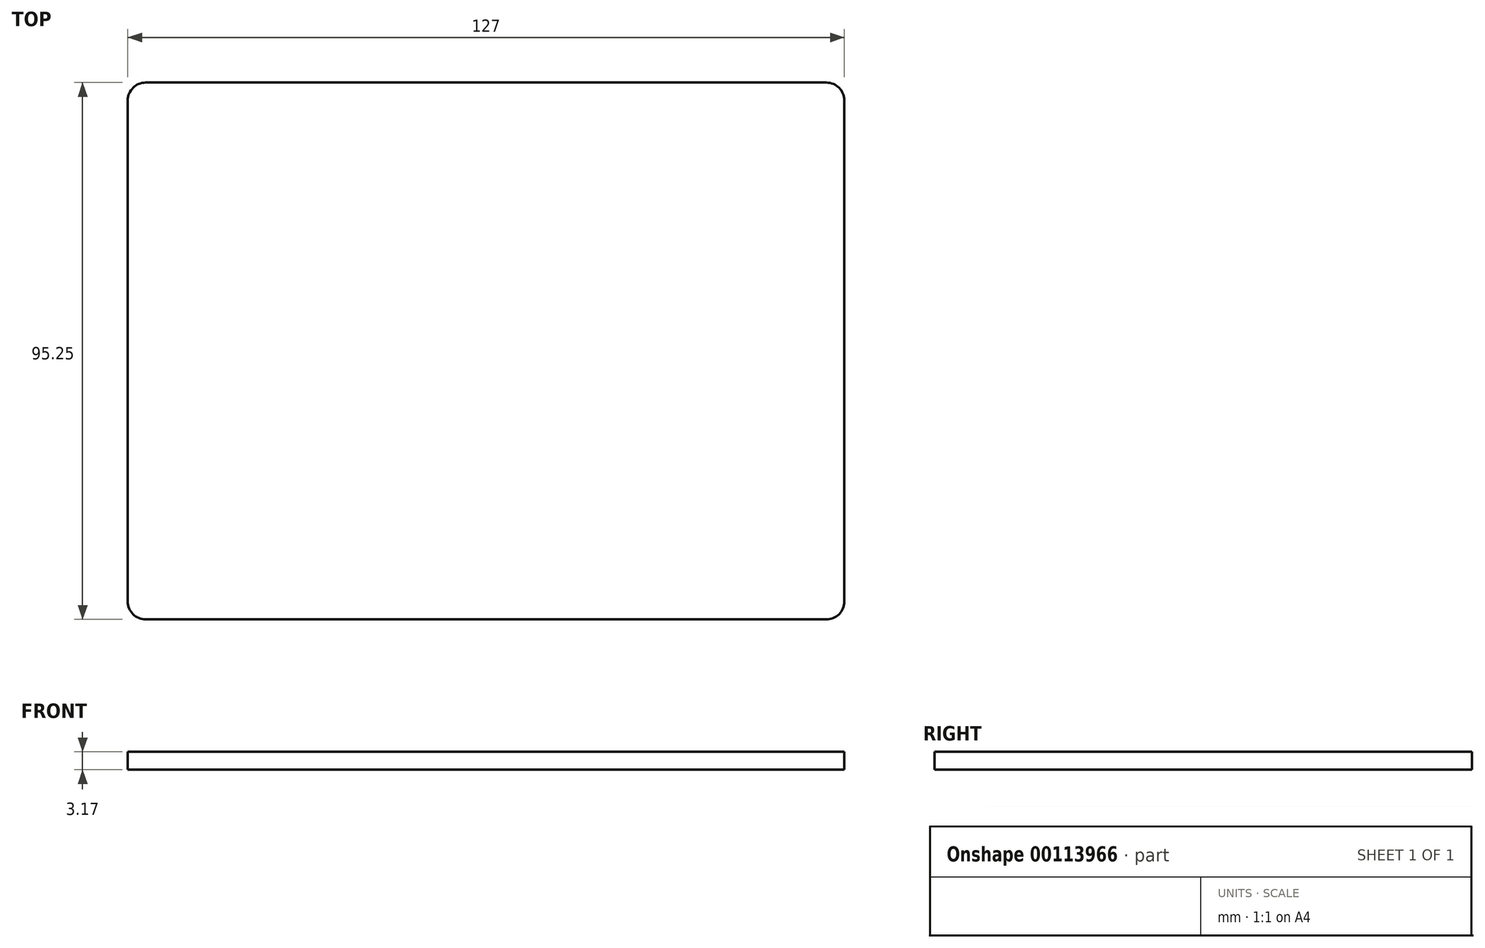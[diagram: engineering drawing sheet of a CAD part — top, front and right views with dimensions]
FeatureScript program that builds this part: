
annotation { "Feature Type Name" : "Feature", "Feature Type Description" : "" }
export const myFeature = defineFeature(function(context is Context, id is Id, definition is map)
    precondition{}
    {
        {
            var Q0;
            Q0=qCreatedBy(makeId("Top.planeOp"),FACE);
            var sketch = newSketch(context, id + "F0", { "sketchPlane" : qUnion([Q0])});
            skLineSegment(sketch, "E0.bottom", {"start": v(3.17, 0) * mm, "end": v(123.83, 0) * mm});
            skLineSegment(sketch, "E0.top", {"start": v(3.17, 95.25) * mm, "end": v(123.82, 95.25) * mm});
            skLineSegment(sketch, "E0.left", {"start": v(0, 3.17) * mm, "end": v(0, 92.08) * mm});
            skLineSegment(sketch, "E0.right", {"start": v(127, 3.17) * mm, "end": v(127, 92.08) * mm});
            skPoint(sketch, "E1.visualSharp", {"position": v(0, 95.25) * mm});
            skArc(sketch, "E1.filletArc", {"start": v(3.17, 95.25) * mm, "mid": v(0.93, 94.32) * mm, "end": v(0, 92.08) * mm});
            skPoint(sketch, "E2.visualSharp", {"position": v(127, 95.25) * mm});
            skArc(sketch, "E2.filletArc", {"start": v(127, 92.08) * mm, "mid": v(126.07, 94.32) * mm, "end": v(123.82, 95.25) * mm});
            skPoint(sketch, "E3.visualSharp", {"position": v(127, 0) * mm});
            skArc(sketch, "E3.filletArc", {"start": v(123.83, 0) * mm, "mid": v(126.07, 0.93) * mm, "end": v(127, 3.18) * mm});
            skPoint(sketch, "E4.visualSharp", {"position": v(0, 0) * mm});
            skArc(sketch, "E4.filletArc", {"start": v(0, 3.17) * mm, "mid": v(0.93, 0.93) * mm, "end": v(3.17, 0) * mm});
            skSolve(sketch);
        }
        {
            var Q0;
            Q0 = qSketchRegion(id + "F0", true);
            extrude(context, id + "F1", {"entities" : qUnion([Q0]), "depth" : 3.17 * mm});
        }
    });
